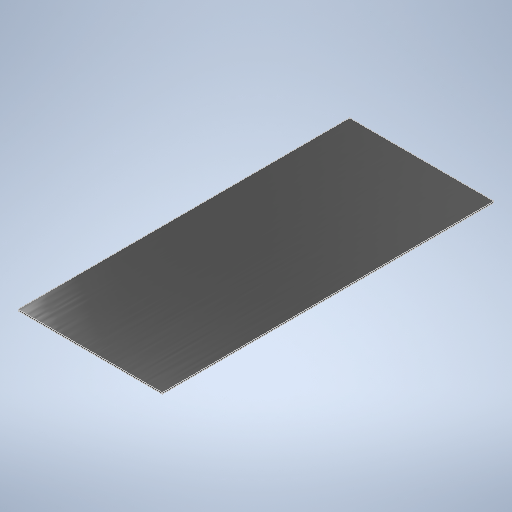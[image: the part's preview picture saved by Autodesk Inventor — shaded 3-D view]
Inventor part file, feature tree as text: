
AUTODESK INVENTOR PART (.ipt)
format: ipt  version: 2025.1 (Build 291241020, 241B)  size: 237,056 bytes
history: native  units: in
note: dims shown in document units (in); Inventor stores cm internally (conversion verified against a paired STEP export)
features: extrude x1, sketch x1
ambient origin geometry x8: Origin, YZ Plane, XZ Plane, XY Plane, X Axis, Y Axis, Z Axis, Center Point
bodies: Solid1 (feature_tree)
feature tree (2):
  extrude  "Extrusion1"  Depth=30.45in
  sketch  "Sketch1"  dims[d0=13.25in d1=30.45in d2=0.125in d3=0.0in]
